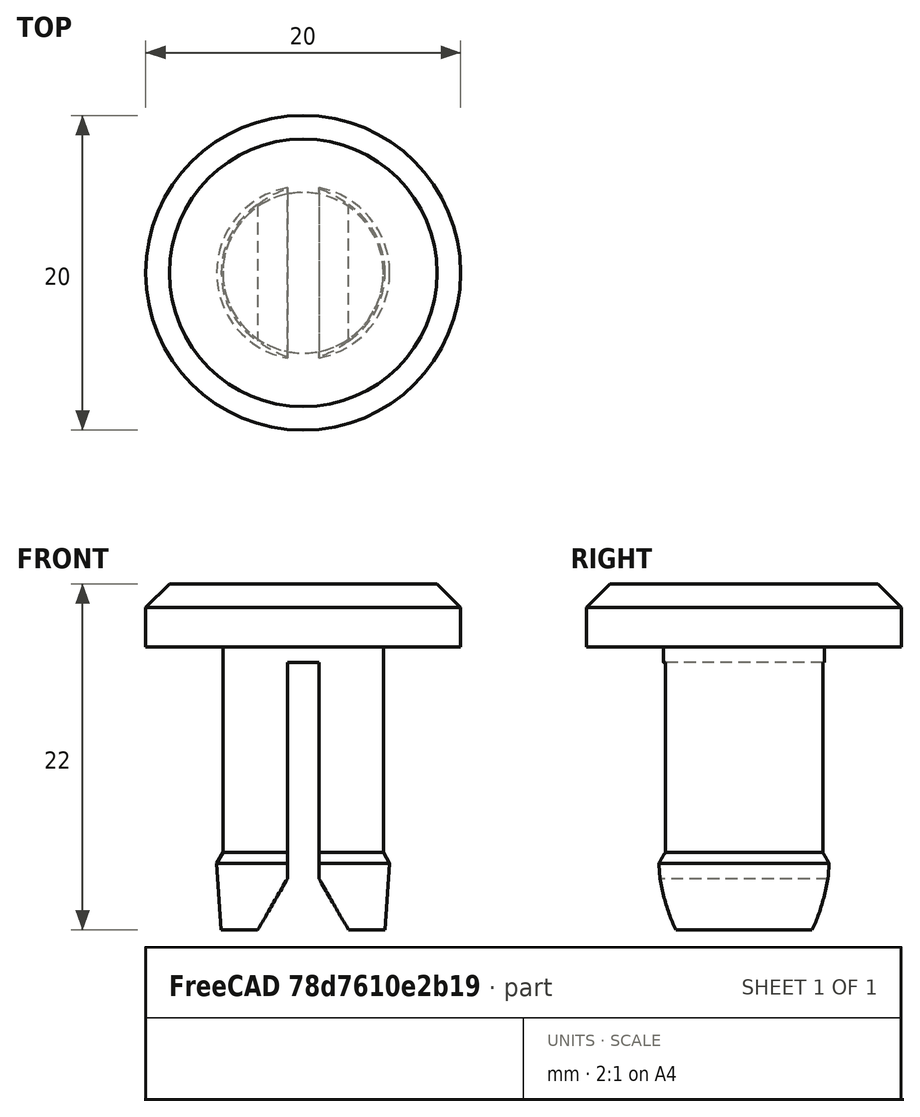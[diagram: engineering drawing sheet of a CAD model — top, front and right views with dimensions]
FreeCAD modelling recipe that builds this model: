
FCSTD DOCUMENT  (FreeCAD 0.16R)
Label: BarPlugs
License: All rights reserved
LicenseURL: http://en.wikipedia.org/wiki/All_rights_reserved
objects: Sketcher::SketchObject×3, Part::Cut×3, PartDesign::Pad×2, PartDesign::Revolution×1, Mesh::Feature×1
note: 12 computed .brp shape members not serialized (recipe doc carries the construction recipe); baked Part::Feature solids carry a one-line shape summary decoded from their .brp

FEATURE [Sketcher::SketchObject] Sketch
  Placement = pos=(0,0,0) rot=(1,0,0;1.5708rad)
  sketch-geometry (9):
    g0: LineSegment StartX=0 StartY=4 StartZ=0 EndX=8.5 EndY=4 EndZ=0
    g1: LineSegment StartX=8.5 StartY=4 StartZ=0 EndX=10 EndY=2.5 EndZ=0
    g2: LineSegment StartX=10 StartY=2.5 StartZ=0 EndX=10 EndY=0 EndZ=0
    g3: LineSegment StartX=10 StartY=0 StartZ=0 EndX=5.1 EndY=0 EndZ=0
    g4: LineSegment StartX=5.20287 StartY=-18 StartZ=0 EndX=0 EndY=-18 EndZ=0
    g5: LineSegment StartX=0 StartY=4 StartZ=0 EndX=0 EndY=-18 EndZ=0
    g6: LineSegment StartX=5.1 StartY=0 StartZ=0 EndX=5.1 EndY=-13.058 EndZ=0
    g7: LineSegment StartX=5.1 StartY=-13.058 StartZ=0 EndX=5.5 EndY=-13.7508 EndZ=0
    g8: LineSegment StartX=5.5 StartY=-13.7508 StartZ=0 EndX=5.20287 EndY=-18 EndZ=0
  constraints (27):
    c: Horizontal(g0)
    c: Coincident(g0,g1)
    c: Coincident(g1,g2)
    c: Coincident(g2,g3)
    c: Horizontal(g4)
    c: Horizontal(g3)
    c: Coincident(g5,g4)
    c: Vertical(g5)
    c: DistanceX(g-1,g5) = 0
    c: DistanceX(g-1,g3) = 5.1
    c: DistanceX(g-1,g2) = 10
    c: Vertical(g2)
    c: PointOnObject(g3,g-1)
    c: DistanceY(g4,g3) = 18
    c: DistanceY(g2,g2) = 2.5
    c: DistanceY(g0) = 4
    c: Angle(g1) = -0.785398
    c: Vertical(g6)
    c: Coincident(g6,g7)
    c: Coincident(g7,g8)
    c: Coincident(g4,g8)
    c: Angle(g8) = -1.64061
    c: Coincident(g6,g3)
    c: Coincident(g5,g0)
    c: DistanceX(g7) = 5.5
    c: Distance(g4) = 5.20287
    c: Angle(g7) = -1.0472
FEATURE [PartDesign::Revolution] Revolution
  Angle = 360
  Axis = (0,0,1)
  Base = (0,0,0)
  Placement = pos=(0,0,0) rot=(1,0,0;1.5708rad)
  ReferenceAxis = -> Sketch [V_Axis]
  Reversed = true
  Sketch = -> Sketch
FEATURE [Sketcher::SketchObject] Sketch001
  Placement = pos=(0,0,0) rot=(1,0,0;1.5708rad)
  sketch-geometry (4):
    g0: LineSegment StartX=8 StartY=-26.8564 StartZ=0 EndX=0 EndY=-13 EndZ=0
    g1: LineSegment StartX=0 StartY=-13 StartZ=0 EndX=-8 EndY=-26.8564 EndZ=0
    g2: LineSegment StartX=-8 StartY=-26.8564 StartZ=0 EndX=8 EndY=-26.8564 EndZ=0
    g3: Circle [constr] CenterX=0 CenterY=-22.2376 CenterZ=0 NormalX=0 NormalY=0 NormalZ=1 Radius=9.2376
  constraints (12):
    c: Coincident(g0,g1)
    c: Coincident(g1,g2)
    c: Coincident(g2,g0)
    c: Equal(g0,g1)
    c: Equal(g0,g2)
    c: PointOnObject(g0,g3)
    c: PointOnObject(g1,g3)
    c: PointOnObject(g2,g3)
    c: Horizontal(g2)
    c: PointOnObject(g0,g-2)
    c: Distance(g1) = 16
    c: DistanceY(g0,g-1) = 13
FEATURE [PartDesign::Pad] Pad
  Length = 15
  Length2 = 100
  Midplane = true
  Placement = pos=(0,0,0) rot=(1,0,0;1.5708rad)
  Sketch = -> Sketch001
  Type = 0
FEATURE [Part::Cut] Cut
  Base = -> Revolution
  Tool = -> Pad
FEATURE [Sketcher::SketchObject] Sketch002
  Placement = pos=(0,0,0) rot=(1,0,0;1.5708rad)
  sketch-geometry (4):
    g0: LineSegment StartX=-1 StartY=-1 StartZ=0 EndX=1 EndY=-1 EndZ=0
    g1: LineSegment StartX=1 StartY=-1 StartZ=0 EndX=1 EndY=-26 EndZ=0
    g2: LineSegment StartX=1 StartY=-26 StartZ=0 EndX=-1 EndY=-26 EndZ=0
    g3: LineSegment StartX=-1 StartY=-26 StartZ=0 EndX=-1 EndY=-1 EndZ=0
  constraints (12):
    c: Coincident(g0,g1)
    c: Coincident(g1,g2)
    c: Coincident(g2,g3)
    c: Coincident(g3,g0)
    c: Horizontal(g0)
    c: Horizontal(g2)
    c: Vertical(g1)
    c: Vertical(g3)
    c: Symmetric(g2,g1,g-2)
    c: DistanceX(g2,g2) = 2
    c: DistanceY(g0) = -1
    c: Distance(g1) = 25
FEATURE [PartDesign::Pad] Pad001
  Length = 30
  Length2 = 100
  Midplane = true
  Placement = pos=(0,0,0) rot=(1,0,0;1.5708rad)
  Sketch = -> Sketch002
  Type = 0
FEATURE [Part::Cut] Cut001
  Base = -> Cut
  Tool = -> Pad001
FEATURE [Part::Cut] Cut002
  Base = -> Cut
  Tool = -> Pad001
FEATURE [Mesh::Feature] Mesh  label="Cut002 (Meshed)"
